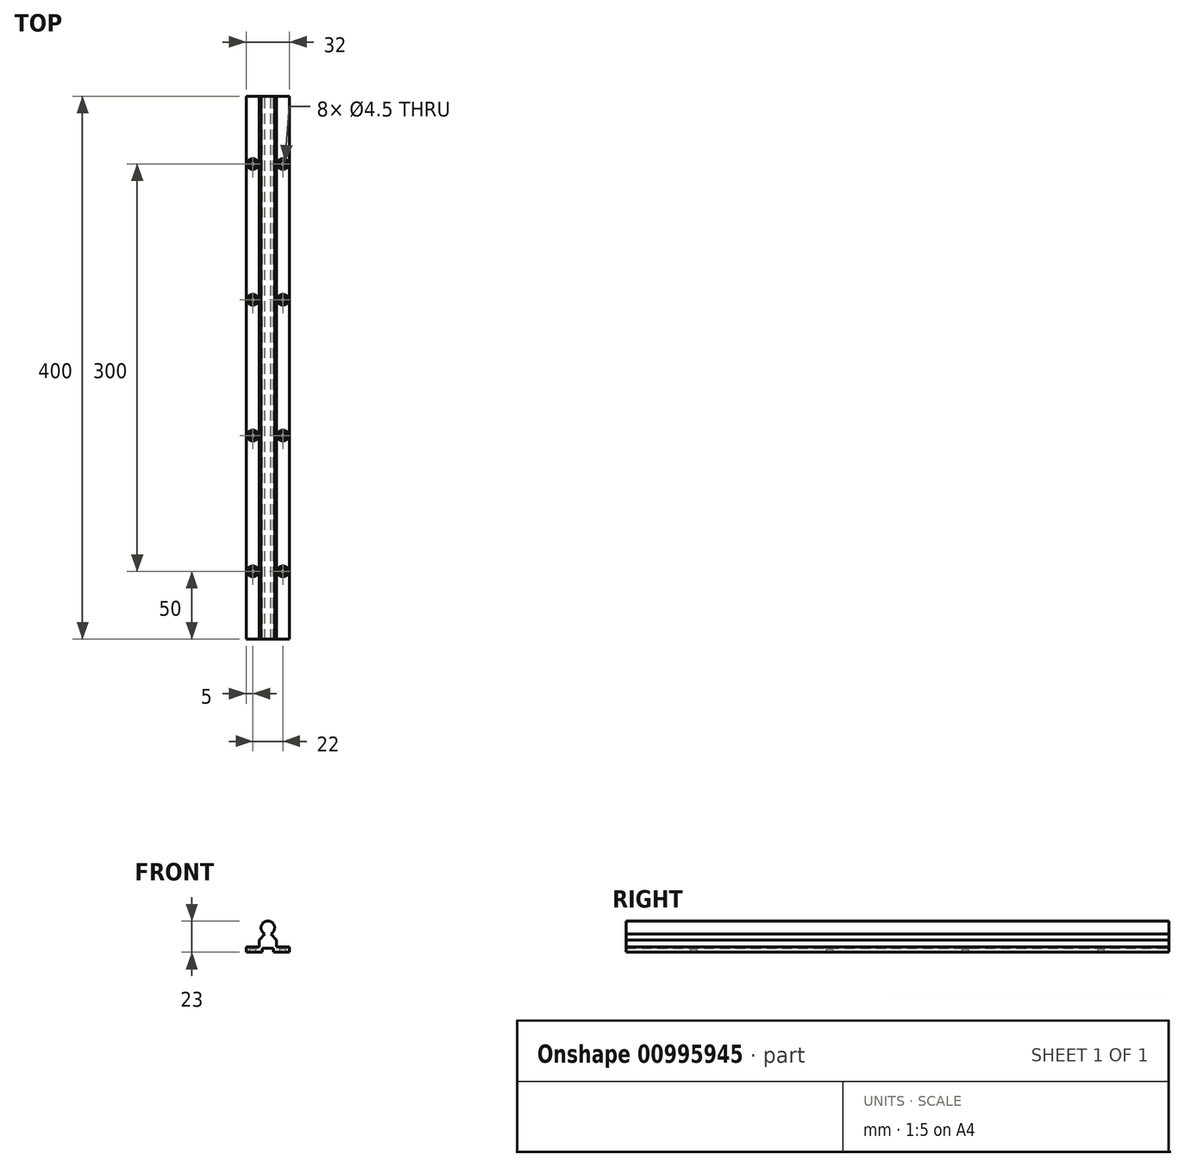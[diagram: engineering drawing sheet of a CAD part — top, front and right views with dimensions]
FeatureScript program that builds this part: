
annotation { "Feature Type Name" : "Feature", "Feature Type Description" : "" }
export const myFeature = defineFeature(function(context is Context, id is Id, definition is map)
    precondition{}
    {
        {
            assignVariable(context, id + "F0", {"name" : "Len", "anyValue" : 400});
        }
        {
            var Q0;
            Q0=qCreatedBy(makeId("Front.planeOp"),FACE);
            var sketch = newSketch(context, id + "F1", { "sketchPlane" : qUnion([Q0])});
            skLineSegment(sketch, "E0.bottom", {"start": v(-16, 0) * mm, "end": v(16, 0) * mm});
            skLineSegment(sketch, "E0.top", {"start": v(-16, 4) * mm, "end": v(16, 4) * mm});
            skLineSegment(sketch, "E0.left", {"start": v(-16, 0) * mm, "end": v(-16, 4) * mm});
            skLineSegment(sketch, "E0.right", {"start": v(16, 0) * mm, "end": v(16, 4) * mm});
            skLineSegment(sketch, "E1.bottom", {"start": v(-6.2, 0) * mm, "end": v(6.2, 0) * mm});
            skLineSegment(sketch, "E1.top", {"start": v(-6.2, 8.9) * mm, "end": v(6.2, 8.9) * mm});
            skLineSegment(sketch, "E1.left", {"start": v(-6.2, 0) * mm, "end": v(-6.2, 8.9) * mm});
            skLineSegment(sketch, "E1.right", {"start": v(6.2, 0) * mm, "end": v(6.2, 8.9) * mm});
            skLineSegment(sketch, "E2", {"start": v(0, 0) * mm, "end": v(0, 26.12) * mm, "construction": true});
            skCircle(sketch, "E3", {"center": v(0, 18) * mm, "radius": 5 * mm});
            skLineSegment(sketch, "E4", {"start": v(6.2, 8.9) * mm, "end": v(2.35, 13.59) * mm});
            skLineSegment(sketch, "E5.MirrorCS", {"start": v(-6.2, 8.9) * mm, "end": v(-2.35, 13.59) * mm});
            skLineSegment(sketch, "E6.bottom", {"start": v(4, 0) * mm, "end": v(-4, 0) * mm});
            skLineSegment(sketch, "E6.top", {"start": v(4, 3) * mm, "end": v(-4, 3) * mm});
            skLineSegment(sketch, "E6.left", {"start": v(4, 0) * mm, "end": v(4, 3) * mm});
            skLineSegment(sketch, "E6.right", {"start": v(-4, 0) * mm, "end": v(-4, 3) * mm});
            skSolve(sketch);
        }
        {
            var Q0;
            Q0=qCreatedBy(makeId("Front.planeOp"),FACE);
            cPlane(context, id + "F2", {"entities" : qUnion([Q0]), "cplaneType" : CPlaneType.OFFSET, "offset" : (getVariable(context, 'Len')) * mm, "width" : 150 * mm, "height" : 150 * mm});
        }
        {
            var Q0;
            {var subQ0=sQuery(id+"F1.wireOp",EDGE,"E0.right");Q0=makeQuery(id+"F1.imprint","IMPRINT",FACE,{"disambiguationData":[TD([[makeQuery(id+"F1.imprint","IMPRINT",EDGE,{"derivedFrom":subQ0}),1.0]])]});}
            var Q1;
            Q1=makeQuery(id+"F1.imprint","IMPRINT",FACE,{"disambiguationData":[TD([[makeQuery(id+"F1.imprint","IMPRINT",EDGE,{"derivedFrom":sQuery(id+"F1.wireOp",EDGE,"E6.top")}),-1.0]])]});
            var Q2;
            {var subQ5=sQuery(id+"F1.wireOp",EDGE,"E1.top");Q2=makeQuery(id+"F1.imprint","IMPRINT",FACE,{"disambiguationData":[TD([[makeQuery(id+"F1.imprint","IMPRINT",EDGE,{"derivedFrom":subQ5}),-1.0]])]});}
            var Q3;
            {var subQ0=sQuery(id+"F1.wireOp",EDGE,"E3");var subQ1=makeQuery(id+"F1.imprint","INTERSECT",VERTEX,{"derivedFrom":[subQ0,sQuery(id+"F1.wireOp",EDGE,"E4")]});Q3=makeQuery(id+"F1.imprint","IMPRINT",FACE,{"disambiguationData":[TD([[makeQuery(id+"F1.imprint","IMPRINT",EDGE,{"disambiguationData":[TD([[subQ1,1.0]])],"derivedFrom":subQ0}),1.0]])]});}
            var Q4;
            {var subQ0=sQuery(id+"F1.wireOp",EDGE,"E0.left");Q4=makeQuery(id+"F1.imprint","IMPRINT",FACE,{"disambiguationData":[TD([[makeQuery(id+"F1.imprint","IMPRINT",EDGE,{"derivedFrom":subQ0}),-1.0]])]});}
            var Q5;
            Q5=makeQuery(id+"F1.imprint","IMPRINT",FACE,{"disambiguationData":[TD([[makeQuery(id+"F1.imprint","IMPRINT",EDGE,{"derivedFrom":sQuery(id+"F1.wireOp",EDGE,"E1.top")}),1.0]])]});
            var Q6;
            Q6=qCreatedBy(id+"F2.planeOp",FACE);
            extrude(context, id + "F3", {"entities" : qUnion([Q0, Q1, Q2, Q3, Q4, Q5]), "endBound" : BoundingType.UP_TO_SURFACE, "depth" : 25 * mm, "endBoundEntityFace" : qUnion([Q6]), "offsetDistance" : 25 * mm});
        }
        {
            var Q0;
            {var subQ0=sQuery(id+"F1.wireOp",EDGE,"E0.top");Q0=makeQuery(id+"F3.opExtrude","SWEPT_FACE",FACE,{"disambiguationData":[OSD([subQ0]),TDD([makeQuery(id+"F1.imprint","IMPRINT",EDGE,{"disambiguationData":[TD([[makeQuery(id+"F1.imprint","INTERSECT",VERTEX,{"derivedFrom":[subQ0,sQuery(id+"F1.wireOp",EDGE,"E0.right")]}),1.0]])],"derivedFrom":subQ0})])]});}
            var sketch = newSketch(context, id + "F4", { "sketchPlane" : qUnion([Q0])});
            skPoint(sketch, "E7", {"position": v(-11, -50) * mm});
            skPoint(sketch, "E8.MirrorP", {"position": v(11, -50) * mm});
            skLineSegment(sketch, "E9", {"start": v(-16.92, -200) * mm, "end": v(16, -200) * mm, "construction": true});
            skPoint(sketch, "E9.startSnap0", {"position": v(16, -200) * mm});
            skPoint(sketch, "E10.0.1.0", {"position": v(-11, -150) * mm});
            skPoint(sketch, "E10.0.1.1", {"position": v(11, -150) * mm});
            skPoint(sketch, "E10.0.2.0", {"position": v(-11, -250) * mm});
            skPoint(sketch, "E10.0.2.1", {"position": v(11, -250) * mm});
            skPoint(sketch, "E10.0.3.0", {"position": v(-11, -350) * mm});
            skPoint(sketch, "E10.0.3.1", {"position": v(11, -350) * mm});
            skPoint(sketch, "E10.0.4.0", {"position": v(-11, -450) * mm});
            skPoint(sketch, "E10.0.4.1", {"position": v(11, -450) * mm});
            skLineSegment(sketch, "E10.direction1", {"start": v(-11, -50) * mm, "end": v(14, -50) * mm, "construction": true});
            skLineSegment(sketch, "E10.direction2", {"start": v(-11, -50) * mm, "end": v(-11, -150) * mm, "construction": true});
            skSolve(sketch);
        }
        {
            var Q0;
            Q0=sQuery(id+"F4.wireOp",VERTEX,"E8.MirrorP");
            var Q1;
            Q1=sQuery(id+"F4.wireOp",VERTEX,"E7");
            var Q2;
            Q2=sQuery(id+"F4.wireOp",VERTEX,"E10.0.1.0");
            var Q3;
            Q3=sQuery(id+"F4.wireOp",VERTEX,"E10.0.1.1");
            var Q4;
            Q4=sQuery(id+"F4.wireOp",VERTEX,"E10.0.2.1");
            var Q5;
            Q5=sQuery(id+"F4.wireOp",VERTEX,"E10.0.2.0");
            var Q6;
            Q6=sQuery(id+"F4.wireOp",VERTEX,"E10.0.3.1");
            var Q7;
            Q7=sQuery(id+"F4.wireOp",VERTEX,"E10.0.3.0");
            var Q8;
            Q8=sQuery(id+"F4.wireOp",VERTEX,"E10.0.4.1");
            var Q9;
            Q9=sQuery(id+"F4.wireOp",VERTEX,"E10.0.4.0");
            var Q10;
            Q10=makeQuery(id+"F3.opExtrude","SWEPT_BODY",BODY,{"disambiguationData":[OSD([sQuery(id+"F1.wireOp",EDGE,"E0.bottom"),sQuery(id+"F1.wireOp",EDGE,"E0.top"),sQuery(id+"F1.wireOp",EDGE,"E0.left"),sQuery(id+"F1.wireOp",EDGE,"E0.right"),sQuery(id+"F1.wireOp",EDGE,"E1.bottom"),sQuery(id+"F1.wireOp",EDGE,"E1.left"),sQuery(id+"F1.wireOp",EDGE,"E1.right"),sQuery(id+"F1.wireOp",EDGE,"E3"),sQuery(id+"F1.wireOp",EDGE,"E4"),sQuery(id+"F1.wireOp",EDGE,"E5.MirrorCS")])]});
            hole(context, id + "F5", {"style" : HoleStyle.C_SINK, "endStyle" : HoleEndStyle.THROUGH, "standardTappedOrClearance" : lookupTablePath({ "standard" : "ISO", "size" : "4.5", "type" : "Drilled" }), "standardBlindInLast" : lookupTablePath({ "standard" : "ISO", "size" : "4.5", "type" : "Drilled" }), "holeDiameter" : 4.5 * mm, "cSinkDiameter" : 8 * mm, "cSinkAngle" : 90 * degree, "majorDiameter" : 5 * mm, "isTappedThrough" : true, "tappedDepth" : 12 * mm, "tapClearance" : 3, "locations" : qUnion([Q0, Q1, Q2, Q3, Q4, Q5, Q6, Q7, Q8, Q9]), "scope" : qUnion([Q10])});
        }
    });
